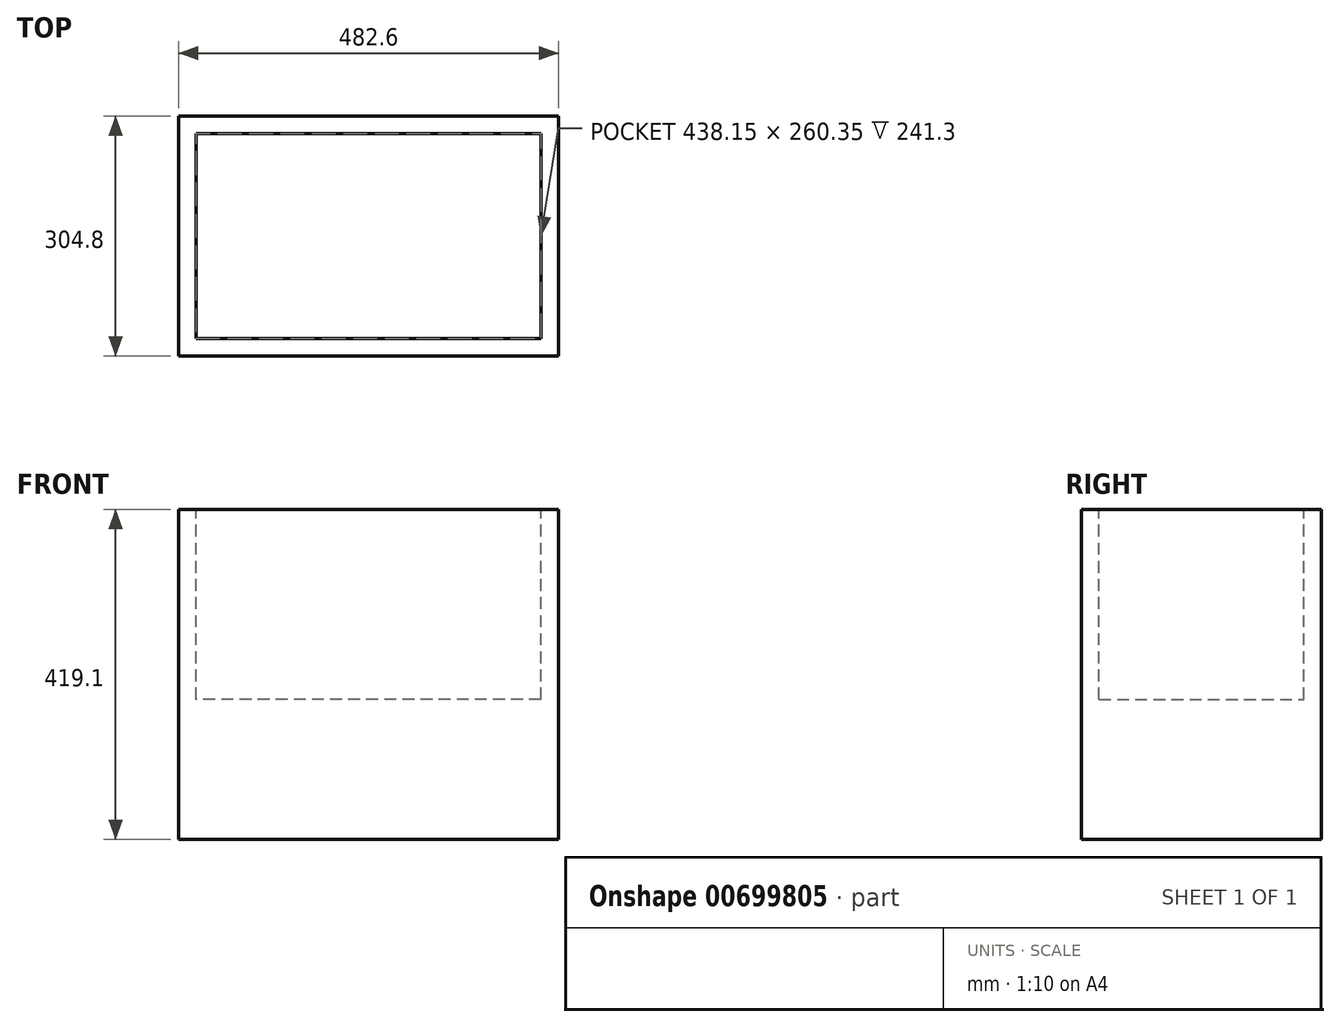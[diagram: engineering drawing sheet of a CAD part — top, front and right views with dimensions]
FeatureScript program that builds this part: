
annotation { "Feature Type Name" : "Feature", "Feature Type Description" : "" }
export const myFeature = defineFeature(function(context is Context, id is Id, definition is map)
    precondition{}
    {
        {
            var Q0;
            Q0=qCreatedBy(makeId("Front.planeOp"),FACE);
            var sketch = newSketch(context, id + "F0", { "sketchPlane" : qUnion([Q0])});
            skLineSegment(sketch, "E0.bottom", {"start": v(241.3, -209.55) * mm, "end": v(-241.3, -209.55) * mm});
            skLineSegment(sketch, "E0.top", {"start": v(241.3, 209.55) * mm, "end": v(-241.3, 209.55) * mm});
            skLineSegment(sketch, "E0.left", {"start": v(241.3, -209.55) * mm, "end": v(241.3, 209.55) * mm});
            skLineSegment(sketch, "E0.right", {"start": v(-241.3, -209.55) * mm, "end": v(-241.3, 209.55) * mm});
            skPoint(sketch, "E0.middle", {"position": v(0, 0) * mm});
            skSolve(sketch);
        }
        {
            var Q0;
            Q0=makeQuery(id+"F0.imprint","IMPRINT",FACE,{"disambiguationData":[TD([[makeQuery(id+"F0.imprint","IMPRINT",EDGE,{"derivedFrom":sQuery(id+"F0.wireOp",EDGE,"E0.bottom")}),-1.0]])]});
            extrude(context, id + "F1", {"entities" : qUnion([Q0]), "endBound" : BoundingType.SYMMETRIC, "depth" : 304.8 * mm, "offsetDistance" : 25.4 * mm});
        }
        {
            var Q0;
            Q0=makeQuery(id+"F1.opExtrude","SWEPT_FACE",FACE,{"disambiguationData":[OSD([sQuery(id+"F0.wireOp",EDGE,"E0.top")])]});
            var sketch = newSketch(context, id + "F2", { "sketchPlane" : qUnion([Q0])});
            skLineSegment(sketch, "E1.bottom", {"start": v(219.07, -130.18) * mm, "end": v(-219.07, -130.18) * mm});
            skLineSegment(sketch, "E1.top", {"start": v(219.07, 130.18) * mm, "end": v(-219.07, 130.18) * mm});
            skLineSegment(sketch, "E1.left", {"start": v(219.07, -130.18) * mm, "end": v(219.07, 130.17) * mm});
            skLineSegment(sketch, "E1.right", {"start": v(-219.07, -130.18) * mm, "end": v(-219.07, 130.17) * mm});
            skPoint(sketch, "E1.middle", {"position": v(0, 0) * mm});
            skSolve(sketch);
        }
        {
            var Q0;
            Q0=makeQuery(id+"F2.imprint","IMPRINT",FACE,{"disambiguationData":[TD([[makeQuery(id+"F2.imprint","IMPRINT",EDGE,{"derivedFrom":sQuery(id+"F2.wireOp",EDGE,"E1.bottom")}),-1.0]])]});
            extrude(context, id + "F3", {"entities" : qUnion([Q0]), "operationType" : NewBodyOperationType.REMOVE, "endBound" : BoundingType.SYMMETRIC, "oppositeDirection" : true, "depth" : 482.6 * mm, "offsetDistance" : 25.4 * mm});
        }
    });
